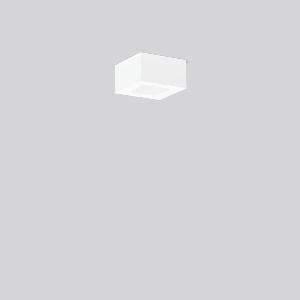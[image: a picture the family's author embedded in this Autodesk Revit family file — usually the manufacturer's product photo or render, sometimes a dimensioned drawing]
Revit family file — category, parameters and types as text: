
# Revit family: toledo_flat_square_a_901551_002_1_5c2d
name_source: partatom
category: Lighting Fixtures
units: mm (PartAtom-declared; Revit-internal decimal feet)

## family parameters
Cut with Voids When Loaded = No
Host = Face
Light Source = No
Part Type = Normal
Room Calculation Point = No
Round Connector Dimension = Use Diameter
Shared = No

## types (1)
- TOLEDO FLAT square A (1 x LED Modul 840, 430 lm, 4000)
    Apparent Load = 5 VA
    CIE Flux Codes = 49 80 96 100 100
    Color Rendering = 80
    Color Temperature = 4000
    Default Elevation = 1800 mm
    Description = Series: TOLEDO FLAT square
Ultra thin surface mounted downlight. Surface mounted housing: sheet steel, powder-coated. Square cover plate: die-cast aluminium, powder coated. Light guide and diffuser made of non-yellowing PMMA, opal matt. Suitable for Ceiling mounting, Wall (surface). Driver integrated. 
Colour: white
Length: 110 mm
Width: 110 mm
Height: 58 mm
Lamp: LED
Socket: without socket
Colour temperature: 4000K
Colour rendering index (CRI): 80
System power: 5 W
Rated luminous flux: 430 lm
Luminous efficiency: 86 lm/W
Control gear: Regulated power supply
Protection class: II
Type of protection: IP 40
    Height = 58 mm
    Lamp = 1 x LED Modul 840
    Lamp Light Flux = 430 lm
    Lamp count = 1
    Length = 110 mm
    Lifetime = 50000 h
    Luminous efficacy = 86 lm/W
    Manufacturer = RZB
    ModVariant = No
    Model = 901551.002.1
    Mounting Place = Ceiling
    Mounting Type = Surface mounted
    Number of Poles = 1
    OnlyDefault = Yes
    Power Factor = 1
    Product Name = TOLEDO FLAT square A
    Product group = Surface mounted downlights
    ProductGroupID = 302
    Protection Class = Protection class II
    Protection Degree = IP 40
    RLX_Detail_Level = 1
    RLX_Emergency_Light_Flux = 0 lm
    RLX_Emergency_Type = 0
    RLX_Emergency_Type_DB = No
    RlxData = <blob elided: 12809 chars, md5=c274c53b>
    Socket = socket
    Standby Power = 0 W
    System Light Flux = 430 lm
    System Power = 5 W
    Type Comments = Product without accessories
    Type Image = 901551.002.jpg
    URL = http://relux.com
    VarID = ---
    Voltage = 230 V
    Voltage Range = 220-240 V
    Weight = 0.00 kg
    Width = 110 mm

## geometry (parser evidence)
native form markers: Sweep x9
no freeform markers — native parametric forms only
